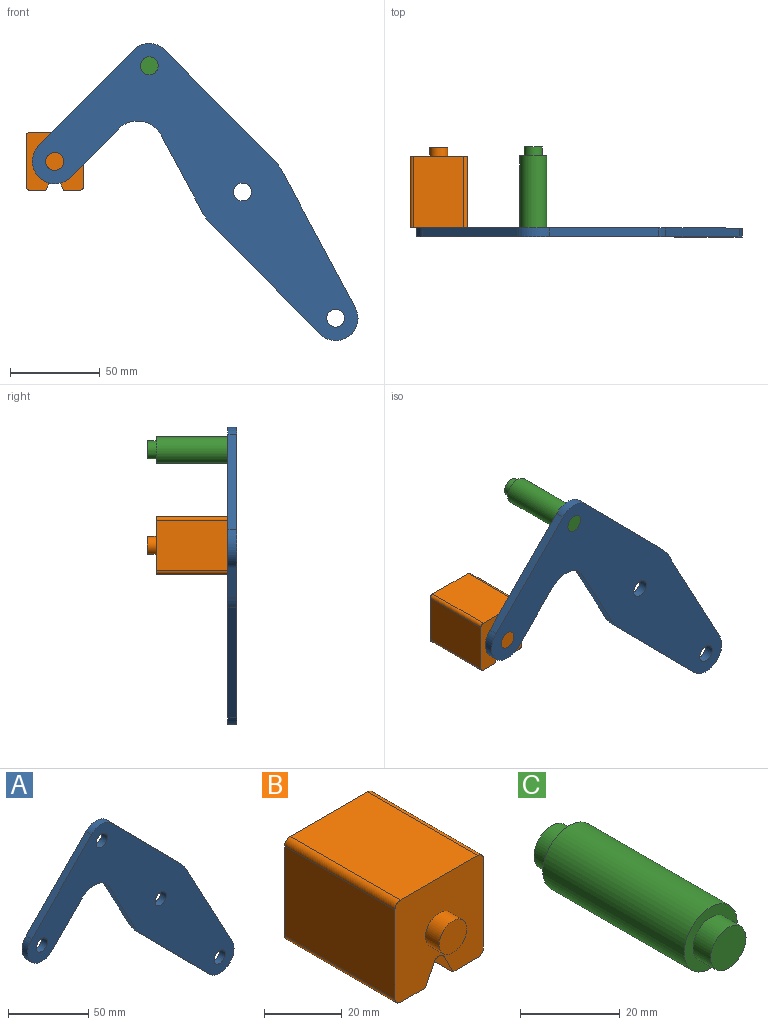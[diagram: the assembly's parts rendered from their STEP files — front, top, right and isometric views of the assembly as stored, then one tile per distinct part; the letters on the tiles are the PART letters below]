
ASSEMBLY  parts=3 mates=1
PART A: 18 faces, bbox 181.7x5x165.8 mm
  f0: plane 43.49x23.35mm, normal (-0.88,0,-0.47), area 246.8mm2, adj f1,f14,f16,f17
  f1: cylinder r=25mm len=5.75mm, axis (0,1,0), area 35.8mm2, adj f0,f2,f16,f17
  f2: plane 61.6x60.87mm, normal (-0.71,0,-0.7), area 433mm2, adj f1,f3,f16,f17
  f3: cylinder r=12.5mm len=21.39mm, axis (0,1,0), area 178.4mm2, adj f2,f4,f16,f17
  f4: plane 76.3x40.96mm, normal (0.88,0,0.47), area 433mm2, adj f3,f5,f16,f17
  f5: cylinder r=25mm len=5.75mm, axis (0,1,0), area 35.8mm2, adj f4,f6,f16,f17
  f6: plane 61.6x60.87mm, normal (0.71,0,0.7), area 433mm2, adj f5,f7,f16,f17
  f7: cylinder r=12.5mm len=17.78mm, axis (0,1,0), area 98.9mm2, adj f6,f8,f16,f17
  f8: plane 53.35x52.71mm, normal (-0.71,0,0.7), area 375mm2, adj f7,f9,f16,f17
  f9: cylinder r=12.5mm len=21.39mm, axis (0,1,0), area 196.3mm2, adj f8,f10,f16,f17
  f10: plane 26.86x26.54mm, normal (0.71,0,-0.7), area 188.8mm2, adj f9,f14,f16,f17
  f11: cylinder r=5mm len=10mm, axis (0,1,0), area 157.1mm2, adj f16,f17
  f12: cylinder r=5mm len=10mm, axis (0,1,0), area 157.1mm2, adj f16,f17
  f13: cylinder r=5mm len=10mm, axis (0,1,0), area 157.1mm2, adj f16,f17
  f14: cylinder r=15mm len=23.89mm, axis (0,1,0), area 140.2mm2, adj f0,f10,f16,f17
  f15: cylinder r=5mm len=10mm, axis (0,1,0), area 157.1mm2, adj f16,f17
  f16: plane 181.66x165.78mm, normal (0,-1,0), area 8710.1mm2, adj f0,f1,f2,f3,f4,f5,f6,f7
  f17: plane 181.66x165.78mm, normal (0,1,0), area 8710.1mm2, adj f0,f1,f2,f3,f4,f5,f6,f7
PART B: 18 faces, bbox 32.1x50x32.1 mm
  f0: plane 40x28.08mm, normal (1,0,0), area 1123.1mm2, adj f4,f10,f13,f14
  f1: plane 40x9.04mm, normal (0,0,-1), area 361.6mm2, adj f2,f4,f10,f14
  f2: plane 40x6.42mm, normal (-0.89,0,-0.45), area 287.2mm2, adj f1,f4,f10,f15
  f3: plane 40x6.42mm, normal (0.89,0,-0.45), area 287.2mm2, adj f4,f5,f10,f15
  f4: plane 32.08x32.08mm, normal (0,-1,0), area 900.6mm2, adj f0,f1,f2,f3,f5,f6,f7,f9
  f5: plane 40x9.04mm, normal (0,0,-1), area 361.6mm2, adj f3,f4,f10,f16
  f6: plane 40x28.08mm, normal (0,0,1), area 1123.1mm2, adj f4,f10,f13,f17
  f7: plane 40x28.08mm, normal (-1,0,0), area 1123.1mm2, adj f4,f10,f16,f17
  f8: plane 10x10mm, normal (0,-1,0), area 78.5mm2, adj f9
  f9: cylinder r=5mm len=10mm, axis (0,1,0), area 157.1mm2, adj f4,f8
  f10: plane 32.08x32.08mm, normal (0,1,0), area 900.6mm2, adj f0,f1,f2,f3,f5,f6,f7,f12
  f11: plane 10x10mm, normal (0,1,0), area 78.5mm2, adj f12
  f12: cylinder r=5mm len=10mm, axis (0,-1,0), area 157.1mm2, adj f10,f11
  f13: cylinder r=2mm len=40mm, axis (0,1,0), area 125.7mm2, adj f0,f4,f6,f10
  f14: cylinder r=2mm len=40mm, axis (0,-1,0), area 125.7mm2, adj f0,f1,f4,f10
  f15: cylinder r=2mm len=40mm, axis (0,1,0), area 177.1mm2, adj f2,f3,f4,f10
  f16: cylinder r=2mm len=40mm, axis (0,1,0), area 125.7mm2, adj f4,f5,f7,f10
  f17: cylinder r=2mm len=40mm, axis (0,-1,0), area 125.7mm2, adj f4,f6,f7,f10
PART C: 7 faces, bbox 15x50x15 mm
  f0: cylinder r=7.5mm len=40mm, axis (0,-1,0), area 1885mm2, adj f2,f5
  f1: cylinder r=5mm len=10mm, axis (0,1,0), area 157.1mm2, adj f2,f3
  f2: plane 15x15mm, normal (0,-1,0), area 98.2mm2, adj f0,f1
  f3: plane 10x10mm, normal (0,-1,0), area 78.5mm2, adj f1
  f4: cylinder r=5mm len=10mm, axis (0,-1,0), area 157.1mm2, adj f5,f6
  f5: plane 15x15mm, normal (0,1,0), area 98.2mm2, adj f0,f4
  f6: plane 10x10mm, normal (0,1,0), area 78.5mm2, adj f4
PLACE A t=(0,5,0)mm fixed
PLACE B t=(0,5,0)mm
PLACE C t=(0,5,0)mm
MATE revolute B.f9 <-> A.f9  axis (0,-1,0) through (-104.69,0,17.04)mm
